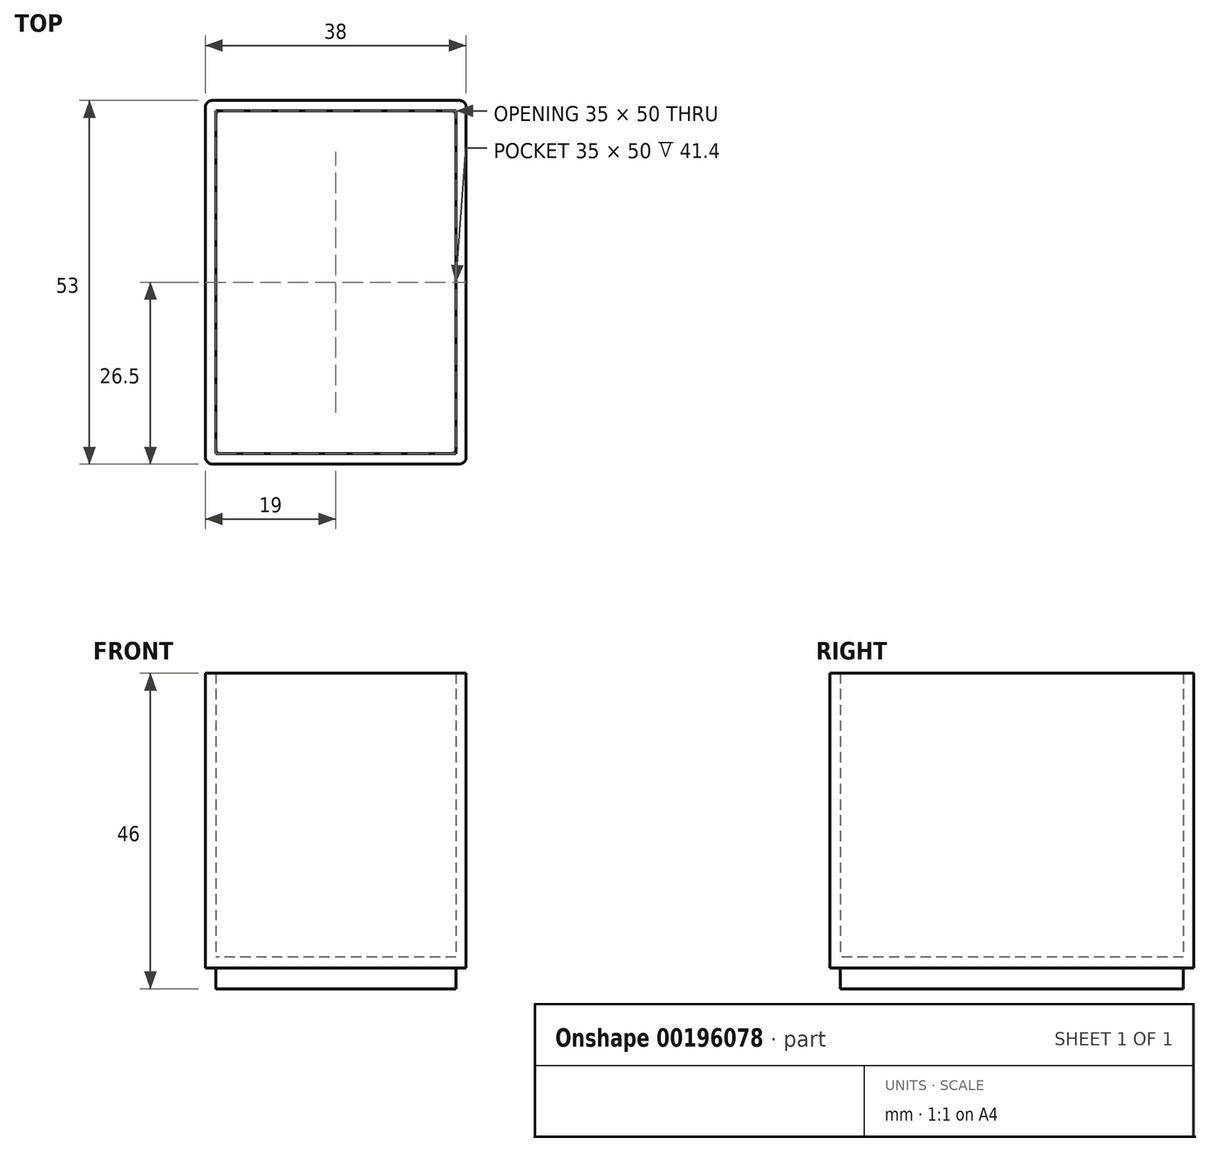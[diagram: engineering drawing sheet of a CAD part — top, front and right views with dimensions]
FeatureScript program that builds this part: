
annotation { "Feature Type Name" : "Feature", "Feature Type Description" : "" }
export const myFeature = defineFeature(function(context is Context, id is Id, definition is map)
    precondition{}
    {
        {
            var Q0;
            Q0=qCreatedBy(makeId("Top.planeOp"),FACE);
            var sketch = newSketch(context, id + "F0", { "sketchPlane" : qUnion([Q0])});
            skLineSegment(sketch, "E0.bottom", {"start": v(0, 0) * mm, "end": v(38, 0) * mm});
            skLineSegment(sketch, "E0.top", {"start": v(0, 53) * mm, "end": v(38, 53) * mm});
            skLineSegment(sketch, "E0.left", {"start": v(0, 0) * mm, "end": v(0, 53) * mm});
            skLineSegment(sketch, "E0.right", {"start": v(38, 0) * mm, "end": v(38, 53) * mm});
            skLineSegment(sketch, "E1.bottom", {"start": v(1.5, 1.5) * mm, "end": v(36.5, 1.5) * mm});
            skLineSegment(sketch, "E1.top", {"start": v(1.5, 51.5) * mm, "end": v(36.5, 51.5) * mm});
            skLineSegment(sketch, "E1.left", {"start": v(1.5, 1.5) * mm, "end": v(1.5, 51.5) * mm});
            skLineSegment(sketch, "E1.right", {"start": v(36.5, 1.5) * mm, "end": v(36.5, 51.5) * mm});
            skSolve(sketch);
        }
        {
            var Q0;
            Q0=makeQuery(id+"F0.imprint","IMPRINT",FACE,{"disambiguationData":[TD([[makeQuery(id+"F0.imprint","IMPRINT",EDGE,{"derivedFrom":sQuery(id+"F0.wireOp",EDGE,"E1.bottom")}),1.0]])]});
            extrude(context, id + "F1", {"entities" : qUnion([Q0]), "oppositeDirection" : true, "depth" : 3 * mm, "offsetDistance" : 25 * mm});
        }
        {
            var Q0;
            Q0=makeQuery(id+"F0.imprint","IMPRINT",FACE,{"disambiguationData":[TD([[makeQuery(id+"F0.imprint","IMPRINT",EDGE,{"derivedFrom":sQuery(id+"F0.wireOp",EDGE,"E0.bottom")}),1.0]])]});
            var Q1;
            Q1=makeQuery(id+"F0.imprint","IMPRINT",FACE,{"disambiguationData":[TD([[makeQuery(id+"F0.imprint","IMPRINT",EDGE,{"derivedFrom":sQuery(id+"F0.wireOp",EDGE,"E1.bottom")}),1.0]])]});
            extrude(context, id + "F2", {"entities" : qUnion([Q0, Q1]), "operationType" : NewBodyOperationType.ADD, "depth" : 1.6 * mm, "offsetDistance" : 25 * mm});
        }
        {
            var Q0;
            Q0=makeQuery(id+"F0.imprint","IMPRINT",FACE,{"disambiguationData":[TD([[makeQuery(id+"F0.imprint","IMPRINT",EDGE,{"derivedFrom":sQuery(id+"F0.wireOp",EDGE,"E0.bottom")}),1.0]])]});
            extrude(context, id + "F3", {"entities" : qUnion([Q0]), "operationType" : NewBodyOperationType.ADD, "depth" : 43 * mm, "offsetDistance" : 25 * mm});
        }
        {
            var Q0;
            Q0=makeQuery(id+"F1.opExtrude","SWEPT_EDGE",EDGE,{"disambiguationData":[OSD([sQuery(id+"F0.wireOp",EDGE,"E1.bottom"),sQuery(id+"F0.wireOp",EDGE,"E1.right")])]});
            var Q1;
            Q1=makeQuery(id+"F1.opExtrude","SWEPT_EDGE",EDGE,{"disambiguationData":[OSD([sQuery(id+"F0.wireOp",EDGE,"E1.bottom"),sQuery(id+"F0.wireOp",EDGE,"E1.left")])]});
            var Q2;
            Q2=makeQuery(id+"F1.opExtrude","SWEPT_EDGE",EDGE,{"disambiguationData":[OSD([sQuery(id+"F0.wireOp",EDGE,"E1.top"),sQuery(id+"F0.wireOp",EDGE,"E1.left")])]});
            var Q3;
            Q3=makeQuery(id+"F1.opExtrude","SWEPT_EDGE",EDGE,{"disambiguationData":[OSD([sQuery(id+"F0.wireOp",EDGE,"E1.top"),sQuery(id+"F0.wireOp",EDGE,"E1.right")])]});
            var Q4;
            {var subQ0=sQuery(id+"F0.wireOp",EDGE,"E0.left");var subQ1=sQuery(id+"F0.wireOp",EDGE,"E0.top");Q4=makeQuery(id+"F3.boolean.opBoolean","MERGE",EDGE,{"derivedFrom":[makeQuery(id+"F2.opExtrude","SWEPT_EDGE",EDGE,{"disambiguationData":[OSD([subQ1,subQ0])]}),makeQuery(id+"F3.opExtrude","SWEPT_EDGE",EDGE,{"disambiguationData":[OSD([subQ1,subQ0])]})]});}
            var Q5;
            {var subQ0=sQuery(id+"F0.wireOp",EDGE,"E0.right");var subQ1=sQuery(id+"F0.wireOp",EDGE,"E0.top");Q5=makeQuery(id+"F3.boolean.opBoolean","MERGE",EDGE,{"derivedFrom":[makeQuery(id+"F2.opExtrude","SWEPT_EDGE",EDGE,{"disambiguationData":[OSD([subQ1,subQ0])]}),makeQuery(id+"F3.opExtrude","SWEPT_EDGE",EDGE,{"disambiguationData":[OSD([subQ1,subQ0])]})]});}
            var Q6;
            {var subQ0=sQuery(id+"F0.wireOp",EDGE,"E0.left");var subQ1=sQuery(id+"F0.wireOp",EDGE,"E0.bottom");Q6=makeQuery(id+"F3.boolean.opBoolean","MERGE",EDGE,{"derivedFrom":[makeQuery(id+"F2.opExtrude","SWEPT_EDGE",EDGE,{"disambiguationData":[OSD([subQ1,subQ0])]}),makeQuery(id+"F3.opExtrude","SWEPT_EDGE",EDGE,{"disambiguationData":[OSD([subQ1,subQ0])]})]});}
            var Q7;
            {var subQ0=sQuery(id+"F0.wireOp",EDGE,"E0.right");var subQ1=sQuery(id+"F0.wireOp",EDGE,"E0.bottom");Q7=makeQuery(id+"F3.boolean.opBoolean","MERGE",EDGE,{"derivedFrom":[makeQuery(id+"F2.opExtrude","SWEPT_EDGE",EDGE,{"disambiguationData":[OSD([subQ1,subQ0])]}),makeQuery(id+"F3.opExtrude","SWEPT_EDGE",EDGE,{"disambiguationData":[OSD([subQ1,subQ0])]})]});}
            fillet(context, id + "F4", {"entities" : qUnion([Q0, Q1, Q2, Q3, Q4, Q5, Q6, Q7]), "radius" : 1 * mm, "tangentPropagation" : true, "allowEdgeOverflow" : false});
        }
    });
